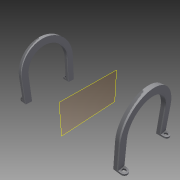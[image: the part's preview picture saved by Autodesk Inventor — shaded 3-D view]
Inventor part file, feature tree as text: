
AUTODESK INVENTOR PART (.ipt)
format: ipt  version: 2014 (Build 180170000, 170)  size: 143,872 bytes
history: native  units: mm
features: extrude x2, sketch x2, mirror x2, revolve x2, plane x1
ambient origin geometry x8: Origin, YZ Plane, XZ Plane, XY Plane, X Axis, Y Axis, Z Axis, Center Point
bodies: Solid1 (feature_tree)
feature tree (9):
  extrude  "Extrusion1"  Depth=4.0mm
  sketch  "Sketch2"  dims[d6=30.0mm d7=8.0mm d8=2.0mm d9=0.0mm d10=5.0mm d13=69.0mm d14=30.0mm d15=0.0mm d16=180.0deg]
  extrude  "Extrusion2"  Depth=8.0mm
  mirror  "Mirror1"
  revolve  "Revolution2"  [1 undecoded]
  plane  "Work Plane1"
  mirror  "Mirror2"
  sketch  "Sketch1"  dims[d0=2.0mm d2=4.0mm]
  revolve  "RevolutionSketch"  [1 undecoded]
note: 2 required parameter values undecoded (feature->parameter linkage not recoverable at this tier; creation-order binding heuristic only, values carry confidence <= 0.55)
